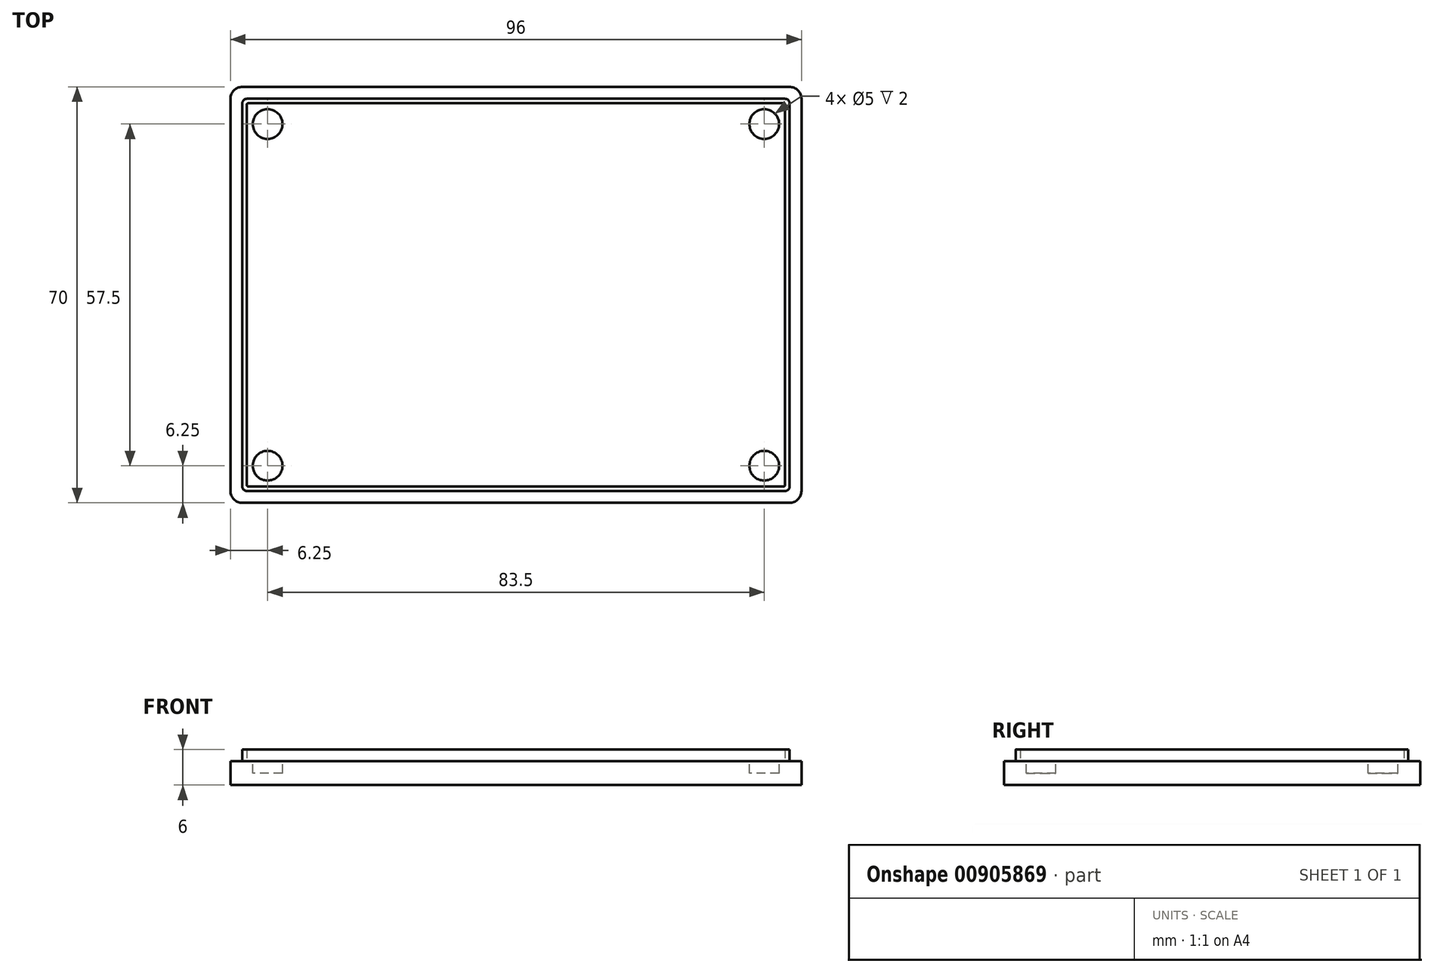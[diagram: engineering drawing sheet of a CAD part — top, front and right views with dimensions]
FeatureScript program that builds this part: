
annotation { "Feature Type Name" : "Feature", "Feature Type Description" : "" }
export const myFeature = defineFeature(function(context is Context, id is Id, definition is map)
    precondition{}
    {
        {
            var Q0;
            Q0=qCreatedBy(makeId("Top.planeOp"),FACE);
            var sketch = newSketch(context, id + "F0", { "sketchPlane" : qUnion([Q0])});
            skLineSegment(sketch, "E0.bottom", {"start": v(-46, 35) * mm, "end": v(46, 35) * mm});
            skLineSegment(sketch, "E0.top", {"start": v(-46, -35) * mm, "end": v(46, -35) * mm});
            skLineSegment(sketch, "E0.left", {"start": v(-48, 33) * mm, "end": v(-48, -33) * mm});
            skLineSegment(sketch, "E0.right", {"start": v(48, 33) * mm, "end": v(48, -33) * mm});
            skPoint(sketch, "E0.middle", {"position": v(0, 0) * mm});
            skPoint(sketch, "E1.visualSharp", {"position": v(-48, 35) * mm});
            skArc(sketch, "E1.filletArc", {"start": v(-46, 35) * mm, "mid": v(-47.41, 34.41) * mm, "end": v(-48, 33) * mm});
            skPoint(sketch, "E2.visualSharp", {"position": v(-48, -35) * mm});
            skArc(sketch, "E2.filletArc", {"start": v(-48, -33) * mm, "mid": v(-47.41, -34.41) * mm, "end": v(-46, -35) * mm});
            skPoint(sketch, "E3.visualSharp", {"position": v(48, -35) * mm});
            skArc(sketch, "E3.filletArc", {"start": v(46, -35) * mm, "mid": v(47.41, -34.41) * mm, "end": v(48, -33) * mm});
            skPoint(sketch, "E4.visualSharp", {"position": v(48, 35) * mm});
            skArc(sketch, "E4.filletArc", {"start": v(48, 33) * mm, "mid": v(47.41, 34.41) * mm, "end": v(46, 35) * mm});
            skSolve(sketch);
        }
        {
            var Q0;
            Q0=makeQuery(id+"F0.imprint","IMPRINT",FACE,{"disambiguationData":[TD([[makeQuery(id+"F0.imprint","IMPRINT",EDGE,{"derivedFrom":sQuery(id+"F0.wireOp",EDGE,"U18dfylj-Norm-gyCY-oxJm-QVkYRqjWbd2D.bottom")}),-1.0]])]});
            var Q1;
            Q1=qSketchRegion(id+"F0",true);
            extrude(context, id + "F1", {"entities" : qUnion([Q0, Q1]), "depth" : 26 * mm, "offsetDistance" : 25 * mm});
        }
        {
            var Q0;
            Q0=makeQuery(id+"F1.opExtrude","CAP_FACE",FACE,{"disambiguationData":[OSD([sQuery(id+"F0.wireOp",EDGE,"E0.bottom"),sQuery(id+"F0.wireOp",EDGE,"E0.top"),sQuery(id+"F0.wireOp",EDGE,"E0.left"),sQuery(id+"F0.wireOp",EDGE,"E0.right"),sQuery(id+"F0.wireOp",EDGE,"E1.filletArc"),sQuery(id+"F0.wireOp",EDGE,"E2.filletArc"),sQuery(id+"F0.wireOp",EDGE,"E3.filletArc"),sQuery(id+"F0.wireOp",EDGE,"E4.filletArc")])],"isStart":false});
            extrude(context, id + "F2", {"entities" : qUnion([Q0]), "depth" : 4 * mm, "offsetDistance" : 25 * mm});
        }
        {
            var Q0;
            Q0=makeQuery(id+"F1.opExtrude","CAP_FACE",FACE,{"disambiguationData":[OSD([sQuery(id+"F0.wireOp",EDGE,"E0.bottom"),sQuery(id+"F0.wireOp",EDGE,"E0.top"),sQuery(id+"F0.wireOp",EDGE,"E0.left"),sQuery(id+"F0.wireOp",EDGE,"E0.right"),sQuery(id+"F0.wireOp",EDGE,"E1.filletArc"),sQuery(id+"F0.wireOp",EDGE,"E2.filletArc"),sQuery(id+"F0.wireOp",EDGE,"E3.filletArc"),sQuery(id+"F0.wireOp",EDGE,"E4.filletArc")])],"isStart":false});
            var sketch = newSketch(context, id + "F3", { "sketchPlane" : qUnion([Q0])});
            skLineSegment(sketch, "E5.bottom", {"start": v(-45, 33) * mm, "end": v(45, 33) * mm});
            skLineSegment(sketch, "E5.top", {"start": v(-45, -33) * mm, "end": v(45, -33) * mm});
            skLineSegment(sketch, "E5.left", {"start": v(-46, 32) * mm, "end": v(-46, -32) * mm});
            skLineSegment(sketch, "E5.right", {"start": v(46, 32) * mm, "end": v(46, -32) * mm});
            skPoint(sketch, "E5.middle", {"position": v(0, 0) * mm});
            skPoint(sketch, "E6.visualSharp", {"position": v(-46, 33) * mm});
            skArc(sketch, "E6.filletArc", {"start": v(-45, 33) * mm, "mid": v(-45.7, 32.7) * mm, "end": v(-46, 32) * mm});
            skPoint(sketch, "E7.visualSharp", {"position": v(46, 33) * mm});
            skArc(sketch, "E7.filletArc", {"start": v(46, 32) * mm, "mid": v(45.7, 32.7) * mm, "end": v(45, 33) * mm});
            skPoint(sketch, "E8.visualSharp", {"position": v(46, -33) * mm});
            skArc(sketch, "E8.filletArc", {"start": v(45, -33) * mm, "mid": v(45.7, -32.7) * mm, "end": v(46, -32) * mm});
            skPoint(sketch, "E9.visualSharp", {"position": v(-46, -33) * mm});
            skArc(sketch, "E9.filletArc", {"start": v(-46, -32) * mm, "mid": v(-45.7, -32.7) * mm, "end": v(-45, -33) * mm});
            skLineSegment(sketch, "E10.bottom", {"start": v(-45, 32) * mm, "end": v(45, 32) * mm});
            skLineSegment(sketch, "E10.top", {"start": v(-45, -32) * mm, "end": v(45, -32) * mm});
            skLineSegment(sketch, "E10.left", {"start": v(-45, 32) * mm, "end": v(-45, -32) * mm});
            skLineSegment(sketch, "E10.right", {"start": v(45, 32) * mm, "end": v(45, -32) * mm});
            skSolve(sketch);
        }
        {
            var Q0;
            Q0=makeQuery(id+"F3.imprint","IMPRINT",FACE,{"disambiguationData":[TD([[makeQuery(id+"F3.imprint","IMPRINT",EDGE,{"derivedFrom":sQuery(id+"F3.wireOp",EDGE,"E5.bottom")}),-1.0]])]});
            extrude(context, id + "F4", {"entities" : qUnion([Q0]), "operationType" : NewBodyOperationType.REMOVE, "oppositeDirection" : true, "depth" : 2 * mm, "offsetDistance" : 25 * mm});
        }
        {
            var Q0;
            Q0=makeQuery(id+"F2.opExtrude","CAP_FACE",FACE,{"disambiguationData":[OSD([sQuery(id+"F0.wireOp",EDGE,"E0.bottom"),sQuery(id+"F0.wireOp",EDGE,"E0.top"),sQuery(id+"F0.wireOp",EDGE,"E0.left"),sQuery(id+"F0.wireOp",EDGE,"E0.right"),sQuery(id+"F0.wireOp",EDGE,"E1.filletArc"),sQuery(id+"F0.wireOp",EDGE,"E2.filletArc"),sQuery(id+"F0.wireOp",EDGE,"E3.filletArc"),sQuery(id+"F0.wireOp",EDGE,"E4.filletArc")])],"isStart":false});
            var sketch = newSketch(context, id + "F5", { "sketchPlane" : qUnion([Q0])});
            skLineSegment(sketch, "E11.bottom", {"start": v(-45.25, 33) * mm, "end": v(45.25, 33) * mm});
            skLineSegment(sketch, "E11.top", {"start": v(-45.25, -33) * mm, "end": v(45.25, -33) * mm});
            skLineSegment(sketch, "E11.left", {"start": v(-46, 32.25) * mm, "end": v(-46, -32.25) * mm});
            skLineSegment(sketch, "E11.right", {"start": v(46, 32.25) * mm, "end": v(46, -32.25) * mm});
            skPoint(sketch, "E11.middle", {"position": v(0, 0) * mm});
            skPoint(sketch, "E12.visualSharp", {"position": v(-46, 33) * mm});
            skArc(sketch, "E12.filletArc", {"start": v(-45.25, 33) * mm, "mid": v(-45.78, 32.78) * mm, "end": v(-46, 32.25) * mm});
            skPoint(sketch, "E13.visualSharp", {"position": v(-46, -33) * mm});
            skArc(sketch, "E13.filletArc", {"start": v(-46, -32.25) * mm, "mid": v(-45.78, -32.78) * mm, "end": v(-45.25, -33) * mm});
            skPoint(sketch, "E14.visualSharp", {"position": v(46, -33) * mm});
            skArc(sketch, "E14.filletArc", {"start": v(45.25, -33) * mm, "mid": v(45.78, -32.78) * mm, "end": v(46, -32.25) * mm});
            skPoint(sketch, "E15.visualSharp", {"position": v(46, 33) * mm});
            skArc(sketch, "E15.filletArc", {"start": v(46, 32.25) * mm, "mid": v(45.78, 32.78) * mm, "end": v(45.25, 33) * mm});
            skLineSegment(sketch, "E16.bottom", {"start": v(-45, 32.25) * mm, "end": v(45, 32.25) * mm});
            skLineSegment(sketch, "E16.top", {"start": v(-45, -32.25) * mm, "end": v(45, -32.25) * mm});
            skLineSegment(sketch, "E16.left", {"start": v(-45.25, 32) * mm, "end": v(-45.25, -32) * mm});
            skLineSegment(sketch, "E16.right", {"start": v(45.25, 32) * mm, "end": v(45.25, -32) * mm});
            skArc(sketch, "E17.filletArc", {"start": v(-45, 32.25) * mm, "mid": v(-45.18, 32.18) * mm, "end": v(-45.25, 32) * mm});
            skArc(sketch, "E18.filletArc", {"start": v(45.25, 32) * mm, "mid": v(45.18, 32.18) * mm, "end": v(45, 32.25) * mm});
            skArc(sketch, "E19.filletArc", {"start": v(45, -32.25) * mm, "mid": v(45.18, -32.18) * mm, "end": v(45.25, -32) * mm});
            skArc(sketch, "E20.filletArc", {"start": v(-45.25, -32) * mm, "mid": v(-45.18, -32.18) * mm, "end": v(-45, -32.25) * mm});
            skSolve(sketch);
        }
        {
            var Q0;
            Q0=makeQuery(id+"F5.imprint","IMPRINT",FACE,{"disambiguationData":[TD([[makeQuery(id+"F5.imprint","IMPRINT",EDGE,{"derivedFrom":sQuery(id+"F5.wireOp",EDGE,"E11.bottom")}),-1.0]])]});
            extrude(context, id + "F6", {"entities" : qUnion([Q0]), "operationType" : NewBodyOperationType.ADD, "depth" : 2 * mm, "offsetDistance" : 25 * mm});
        }
        {
            var Q0;
            Q0=makeQuery(id+"F4.boolean.opBoolean","SPLIT",FACE,{"disambiguationData":[TD([makeQuery(id+"F4.opExtrude","SWEPT_FACE",FACE,{"disambiguationData":[OSD([sQuery(id+"F3.wireOp",EDGE,"E10.bottom")])]})])],"derivedFrom":makeQuery(id+"F1.opExtrude","CAP_FACE",FACE,{"disambiguationData":[OSD([sQuery(id+"F0.wireOp",EDGE,"E0.bottom"),sQuery(id+"F0.wireOp",EDGE,"E0.top"),sQuery(id+"F0.wireOp",EDGE,"E0.left"),sQuery(id+"F0.wireOp",EDGE,"E0.right"),sQuery(id+"F0.wireOp",EDGE,"E1.filletArc"),sQuery(id+"F0.wireOp",EDGE,"E2.filletArc"),sQuery(id+"F0.wireOp",EDGE,"E3.filletArc"),sQuery(id+"F0.wireOp",EDGE,"E4.filletArc")])],"isStart":false})});
            var sketch = newSketch(context, id + "F7", { "sketchPlane" : qUnion([Q0])});
            skCircle(sketch, "E21", {"center": v(-41.5, -28.5) * mm, "radius": 2.5 * mm});
            skCircle(sketch, "E22", {"center": v(-41.5, 28.5) * mm, "radius": 2.5 * mm});
            skCircle(sketch, "E23", {"center": v(41.5, 28.5) * mm, "radius": 2.5 * mm});
            skCircle(sketch, "E24", {"center": v(41.5, -28.5) * mm, "radius": 2.5 * mm});
            skSolve(sketch);
        }
        {
            var Q0;
            Q0=makeQuery(id+"F7.imprint","IMPRINT",FACE,{"disambiguationData":[TD([[makeQuery(id+"F7.imprint","IMPRINT",EDGE,{"derivedFrom":sQuery(id+"F7.wireOp",EDGE,"E21")}),1.0]])]});
            var Q1;
            Q1=makeQuery(id+"F7.imprint","IMPRINT",FACE,{"disambiguationData":[TD([[makeQuery(id+"F7.imprint","IMPRINT",EDGE,{"derivedFrom":sQuery(id+"F7.wireOp",EDGE,"E22")}),1.0]])]});
            var Q2;
            Q2=makeQuery(id+"F7.imprint","IMPRINT",FACE,{"disambiguationData":[TD([[makeQuery(id+"F7.imprint","IMPRINT",EDGE,{"derivedFrom":sQuery(id+"F7.wireOp",EDGE,"E23")}),1.0]])]});
            var Q3;
            Q3=makeQuery(id+"F7.imprint","IMPRINT",FACE,{"disambiguationData":[TD([[makeQuery(id+"F7.imprint","IMPRINT",EDGE,{"derivedFrom":sQuery(id+"F7.wireOp",EDGE,"E24")}),1.0]])]});
            extrude(context, id + "F8", {"entities" : qUnion([Q0, Q1, Q2, Q3]), "operationType" : NewBodyOperationType.REMOVE, "oppositeDirection" : true, "depth" : 2 * mm, "offsetDistance" : 25 * mm});
        }
        {
            var Q0;
            Q0=makeQuery(id+"F6.boolean.opBoolean","SPLIT",FACE,{"disambiguationData":[TD([makeQuery(id+"F6.opExtrude","SWEPT_FACE",FACE,{"disambiguationData":[OSD([sQuery(id+"F5.wireOp",EDGE,"E16.bottom")])]})])],"derivedFrom":makeQuery(id+"F2.opExtrude","CAP_FACE",FACE,{"disambiguationData":[OSD([sQuery(id+"F0.wireOp",EDGE,"E0.bottom"),sQuery(id+"F0.wireOp",EDGE,"E0.top"),sQuery(id+"F0.wireOp",EDGE,"E0.left"),sQuery(id+"F0.wireOp",EDGE,"E0.right"),sQuery(id+"F0.wireOp",EDGE,"E1.filletArc"),sQuery(id+"F0.wireOp",EDGE,"E2.filletArc"),sQuery(id+"F0.wireOp",EDGE,"E3.filletArc"),sQuery(id+"F0.wireOp",EDGE,"E4.filletArc")])],"isStart":false})});
            var sketch = newSketch(context, id + "F9", { "sketchPlane" : qUnion([Q0])});
            skCircle(sketch, "E25", {"center": v(-41.75, 28.75) * mm, "radius": 2.5 * mm});
            skCircle(sketch, "E26", {"center": v(-41.75, -28.75) * mm, "radius": 2.5 * mm});
            skCircle(sketch, "E27", {"center": v(41.75, -28.75) * mm, "radius": 2.5 * mm});
            skCircle(sketch, "E28", {"center": v(41.75, 28.75) * mm, "radius": 2.5 * mm});
            skSolve(sketch);
        }
        {
            var Q0;
            Q0=makeQuery(id+"F9.imprint","IMPRINT",FACE,{"disambiguationData":[TD([[makeQuery(id+"F9.imprint","IMPRINT",EDGE,{"derivedFrom":sQuery(id+"F9.wireOp",EDGE,"E26")}),1.0]])]});
            var Q1;
            Q1=makeQuery(id+"F9.imprint","IMPRINT",FACE,{"disambiguationData":[TD([[makeQuery(id+"F9.imprint","IMPRINT",EDGE,{"derivedFrom":sQuery(id+"F9.wireOp",EDGE,"E25")}),1.0]])]});
            var Q2;
            Q2=makeQuery(id+"F9.imprint","IMPRINT",FACE,{"disambiguationData":[TD([[makeQuery(id+"F9.imprint","IMPRINT",EDGE,{"derivedFrom":sQuery(id+"F9.wireOp",EDGE,"E28")}),1.0]])]});
            var Q3;
            Q3=makeQuery(id+"F9.imprint","IMPRINT",FACE,{"disambiguationData":[TD([[makeQuery(id+"F9.imprint","IMPRINT",EDGE,{"derivedFrom":sQuery(id+"F9.wireOp",EDGE,"E27")}),1.0]])]});
            extrude(context, id + "F10", {"entities" : qUnion([Q0, Q1, Q2, Q3]), "operationType" : NewBodyOperationType.REMOVE, "oppositeDirection" : true, "depth" : 2 * mm, "offsetDistance" : 25 * mm});
        }
        {
            var Q0;
            Q0=makeQuery(id+"F4.boolean.opBoolean","SPLIT",FACE,{"disambiguationData":[TD([makeQuery(id+"F4.opExtrude","SWEPT_FACE",FACE,{"disambiguationData":[OSD([sQuery(id+"F3.wireOp",EDGE,"E10.bottom")])]})])],"derivedFrom":makeQuery(id+"F1.opExtrude","CAP_FACE",FACE,{"disambiguationData":[OSD([sQuery(id+"F0.wireOp",EDGE,"E0.bottom"),sQuery(id+"F0.wireOp",EDGE,"E0.top"),sQuery(id+"F0.wireOp",EDGE,"E0.left"),sQuery(id+"F0.wireOp",EDGE,"E0.right"),sQuery(id+"F0.wireOp",EDGE,"E1.filletArc"),sQuery(id+"F0.wireOp",EDGE,"E2.filletArc"),sQuery(id+"F0.wireOp",EDGE,"E3.filletArc"),sQuery(id+"F0.wireOp",EDGE,"E4.filletArc")])],"isStart":false})});
            var sketch = newSketch(context, id + "F11", { "sketchPlane" : qUnion([Q0])});
            skLineSegment(sketch, "E29.bottom", {"start": v(-43, -25) * mm, "end": v(43, -25) * mm});
            skLineSegment(sketch, "E29.top", {"start": v(-43, 25) * mm, "end": v(43, 25) * mm});
            skLineSegment(sketch, "E29.left", {"start": v(-43, -25) * mm, "end": v(-43, 25) * mm});
            skLineSegment(sketch, "E29.right", {"start": v(43, -25) * mm, "end": v(43, 25) * mm});
            skPoint(sketch, "E29.middle", {"position": v(0, 0) * mm});
            skLineSegment(sketch, "E30.bottom", {"start": v(-38, -30) * mm, "end": v(38, -30) * mm});
            skLineSegment(sketch, "E30.top", {"start": v(-38, 30) * mm, "end": v(38, 30) * mm});
            skLineSegment(sketch, "E30.left", {"start": v(-38, -30) * mm, "end": v(-38, 30) * mm});
            skLineSegment(sketch, "E30.right", {"start": v(38, -30) * mm, "end": v(38, 30) * mm});
            skSolve(sketch);
        }
        {
            var Q0;
            {var subQ0=sQuery(id+"F11.wireOp",EDGE,"E29.left");Q0=makeQuery(id+"F11.imprint","IMPRINT",FACE,{"disambiguationData":[TD([[makeQuery(id+"F11.imprint","IMPRINT",EDGE,{"derivedFrom":subQ0}),-1.0]])]});}
            var Q1;
            {var subQ5=sQuery(id+"F11.wireOp",EDGE,"E30.bottom");Q1=makeQuery(id+"F11.imprint","IMPRINT",FACE,{"disambiguationData":[TD([[makeQuery(id+"F11.imprint","IMPRINT",EDGE,{"derivedFrom":subQ5}),1.0]])]});}
            var Q2;
            {var subQ0=sQuery(id+"F11.wireOp",EDGE,"E30.left");var subQ1=sQuery(id+"F11.wireOp",EDGE,"E29.bottom");var subQ2=makeQuery(id+"F11.imprint","INTERSECT",VERTEX,{"derivedFrom":[subQ1,subQ0]});Q2=makeQuery(id+"F11.imprint","IMPRINT",FACE,{"disambiguationData":[TD([[makeQuery(id+"F11.imprint","IMPRINT",EDGE,{"disambiguationData":[TD([[subQ2,-1.0]])],"derivedFrom":subQ1}),1.0]])]});}
            var Q3;
            {var subQ5=sQuery(id+"F11.wireOp",EDGE,"E30.top");Q3=makeQuery(id+"F11.imprint","IMPRINT",FACE,{"disambiguationData":[TD([[makeQuery(id+"F11.imprint","IMPRINT",EDGE,{"derivedFrom":subQ5}),-1.0]])]});}
            var Q4;
            {var subQ0=sQuery(id+"F11.wireOp",EDGE,"E29.right");Q4=makeQuery(id+"F11.imprint","IMPRINT",FACE,{"disambiguationData":[TD([[makeQuery(id+"F11.imprint","IMPRINT",EDGE,{"derivedFrom":subQ0}),1.0]])]});}
            extrude(context, id + "F12", {"entities" : qUnion([Q0, Q1, Q2, Q3, Q4]), "operationType" : NewBodyOperationType.REMOVE, "oppositeDirection" : true, "depth" : 22 * mm, "offsetDistance" : 25 * mm});
        }
        {
            var Q0;
            Q0=makeQuery(id+"F1.opExtrude","SWEPT_FACE",FACE,{"disambiguationData":[OSD([sQuery(id+"F0.wireOp",EDGE,"E0.right")])]});
            var sketch = newSketch(context, id + "F13", { "sketchPlane" : qUnion([Q0])});
            skPoint(sketch, "E31.centerSnap0", {"position": v(-33, 13) * mm});
            skCircle(sketch, "E32", {"center": v(8, 14.5) * mm, "radius": 1 * mm});
            skPoint(sketch, "E32.centerSnap0", {"position": v(0, 0) * mm});
            skCircle(sketch, "E33", {"center": v(11, 14.5) * mm, "radius": 1 * mm});
            skCircle(sketch, "E34", {"center": v(14, 14.5) * mm, "radius": 1 * mm});
            skCircle(sketch, "E35", {"center": v(8, 11.5) * mm, "radius": 1 * mm});
            skCircle(sketch, "E36", {"center": v(11, 11.5) * mm, "radius": 1 * mm});
            skCircle(sketch, "E37", {"center": v(14, 11.5) * mm, "radius": 1 * mm});
            skSolve(sketch);
        }
        {
            var Q0;
            Q0=makeQuery(id+"F13.imprint","IMPRINT",FACE,{"disambiguationData":[TD([[makeQuery(id+"F13.imprint","IMPRINT",EDGE,{"derivedFrom":sQuery(id+"F13.wireOp",EDGE,"E32")}),1.0]])]});
            var Q1;
            Q1=makeQuery(id+"F13.imprint","IMPRINT",FACE,{"disambiguationData":[TD([[makeQuery(id+"F13.imprint","IMPRINT",EDGE,{"derivedFrom":sQuery(id+"F13.wireOp",EDGE,"E35")}),1.0]])]});
            var Q2;
            Q2=makeQuery(id+"F13.imprint","IMPRINT",FACE,{"disambiguationData":[TD([[makeQuery(id+"F13.imprint","IMPRINT",EDGE,{"derivedFrom":sQuery(id+"F13.wireOp",EDGE,"E36")}),1.0]])]});
            var Q3;
            Q3=makeQuery(id+"F13.imprint","IMPRINT",FACE,{"disambiguationData":[TD([[makeQuery(id+"F13.imprint","IMPRINT",EDGE,{"derivedFrom":sQuery(id+"F13.wireOp",EDGE,"E33")}),1.0]])]});
            var Q4;
            Q4=makeQuery(id+"F13.imprint","IMPRINT",FACE,{"disambiguationData":[TD([[makeQuery(id+"F13.imprint","IMPRINT",EDGE,{"derivedFrom":sQuery(id+"F13.wireOp",EDGE,"E34")}),1.0]])]});
            var Q5;
            Q5=makeQuery(id+"F13.imprint","IMPRINT",FACE,{"disambiguationData":[TD([[makeQuery(id+"F13.imprint","IMPRINT",EDGE,{"derivedFrom":sQuery(id+"F13.wireOp",EDGE,"E37")}),1.0]])]});
            extrude(context, id + "F14", {"entities" : qUnion([Q0, Q1, Q2, Q3, Q4, Q5]), "operationType" : NewBodyOperationType.REMOVE, "endBound" : BoundingType.UP_TO_NEXT, "oppositeDirection" : true, "depth" : 25 * mm, "offsetDistance" : 25 * mm});
        }
        {
            var Q0;
            Q0=makeQuery(id+"F1.opExtrude","SWEPT_FACE",FACE,{"disambiguationData":[OSD([sQuery(id+"F0.wireOp",EDGE,"E0.left")])]});
            var sketch = newSketch(context, id + "F15", { "sketchPlane" : qUnion([Q0])});
            skCircle(sketch, "E38", {"center": v(7, 12.5) * mm, "radius": 5 * mm});
            skCircle(sketch, "E39", {"center": v(7, 12.5) * mm, "radius": 11 * mm});
            skSolve(sketch);
        }
        {
            var Q0;
            Q0=makeQuery(id+"F15.imprint","IMPRINT",FACE,{"disambiguationData":[TD([[makeQuery(id+"F15.imprint","IMPRINT",EDGE,{"derivedFrom":sQuery(id+"F15.wireOp",EDGE,"E38")}),-1.0]])]});
            extrude(context, id + "F16", {"entities" : qUnion([Q0]), "operationType" : NewBodyOperationType.REMOVE, "oppositeDirection" : true, "depth" : 2 * mm, "offsetDistance" : 25 * mm});
        }
        {
            var Q0;
            Q0=makeQuery(id+"F15.imprint","IMPRINT",FACE,{"disambiguationData":[TD([[makeQuery(id+"F15.imprint","IMPRINT",EDGE,{"derivedFrom":sQuery(id+"F15.wireOp",EDGE,"E38")}),1.0]])]});
            extrude(context, id + "F17", {"entities" : qUnion([Q0]), "operationType" : NewBodyOperationType.REMOVE, "endBound" : BoundingType.UP_TO_NEXT, "oppositeDirection" : true, "depth" : 25 * mm, "offsetDistance" : 25 * mm});
        }
        {
            var Q0;
            Q0=makeQuery(id+"F1.opExtrude","SWEPT_FACE",FACE,{"disambiguationData":[OSD([sQuery(id+"F0.wireOp",EDGE,"E0.top")])]});
            var sketch = newSketch(context, id + "F18", { "sketchPlane" : qUnion([Q0])});
            skLineSegment(sketch, "E40.bottom", {"start": v(-33, 22) * mm, "end": v(33, 22) * mm});
            skLineSegment(sketch, "E40.top", {"start": v(-33, 4) * mm, "end": v(33, 4) * mm});
            skLineSegment(sketch, "E40.left", {"start": v(-33, 22) * mm, "end": v(-33, 4) * mm});
            skLineSegment(sketch, "E40.right", {"start": v(33, 22) * mm, "end": v(33, 4) * mm});
            skPoint(sketch, "E40.middle", {"position": v(0, 13) * mm});
            skPoint(sketch, "E40.middle.positionSnap0", {"position": v(-46, 13) * mm});
            skPoint(sketch, "E40.centerSnap0", {"position": v(-46, 13) * mm});
            skLineSegment(sketch, "E41.bottom", {"start": v(29.73, 17) * mm, "end": v(28.83, 17) * mm});
            skLineSegment(sketch, "E41.top", {"start": v(29.73, 9) * mm, "end": v(28.83, 9) * mm});
            skLineSegment(sketch, "E41.left", {"start": v(30.73, 16) * mm, "end": v(30.73, 10) * mm});
            skLineSegment(sketch, "E41.right", {"start": v(27.83, 16) * mm, "end": v(27.83, 10) * mm});
            skPoint(sketch, "E41.middle", {"position": v(29.28, 13) * mm});
            skPoint(sketch, "E41.middle.positionSnap0", {"position": v(33, 13) * mm});
            skPoint(sketch, "E41.centerSnap0", {"position": v(33, 13) * mm});
            skPoint(sketch, "E42.visualSharp", {"position": v(27.83, 9) * mm});
            skArc(sketch, "E42.filletArc", {"start": v(27.83, 10) * mm, "mid": v(28.12, 9.3) * mm, "end": v(28.83, 9) * mm});
            skPoint(sketch, "E43.visualSharp", {"position": v(27.83, 17) * mm});
            skArc(sketch, "E43.filletArc", {"start": v(28.83, 17) * mm, "mid": v(28.12, 16.7) * mm, "end": v(27.83, 16) * mm});
            skPoint(sketch, "E44.visualSharp", {"position": v(30.73, 17) * mm});
            skArc(sketch, "E44.filletArc", {"start": v(30.73, 16) * mm, "mid": v(30.44, 16.7) * mm, "end": v(29.73, 17) * mm});
            skPoint(sketch, "E45.visualSharp", {"position": v(30.73, 9) * mm});
            skArc(sketch, "E45.filletArc", {"start": v(29.73, 9) * mm, "mid": v(30.44, 9.3) * mm, "end": v(30.73, 10) * mm});
            skCircle(sketch, "E46", {"center": v(24.1, 13) * mm, "radius": 2 * mm});
            skCircle(sketch, "E47", {"center": v(17.55, 13) * mm, "radius": 2 * mm});
            skCircle(sketch, "E48", {"center": v(11, 13) * mm, "radius": 2 * mm});
            skCircle(sketch, "E49", {"center": v(-29, 13) * mm, "radius": 3 * mm});
            skCircle(sketch, "E50", {"center": v(-30.34, 6.5) * mm, "radius": 1.8 * mm});
            skCircle(sketch, "E51", {"center": v(-30.34, 6.5) * mm, "radius": 0.8 * mm});
            skCircle(sketch, "E52", {"center": v(-30.34, 19.5) * mm, "radius": 1.8 * mm});
            skCircle(sketch, "E53", {"center": v(-30.34, 19.5) * mm, "radius": 0.8 * mm});
            skCircle(sketch, "E54", {"center": v(23.84, 19.5) * mm, "radius": 1.8 * mm});
            skCircle(sketch, "E55", {"center": v(23.84, 19.5) * mm, "radius": 0.8 * mm});
            skLineSegment(sketch, "E56.bottom", {"start": v(5.2, 7.24) * mm, "end": v(-14.97, 7.24) * mm});
            skLineSegment(sketch, "E56.top", {"start": v(5.2, 18.76) * mm, "end": v(-14.97, 18.76) * mm});
            skLineSegment(sketch, "E56.left", {"start": v(5.2, 7.24) * mm, "end": v(5.2, 18.76) * mm});
            skLineSegment(sketch, "E56.right", {"start": v(-14.97, 7.24) * mm, "end": v(-14.97, 18.76) * mm});
            skPoint(sketch, "E56.middle", {"position": v(-4.89, 13) * mm});
            skSolve(sketch);
        }
        {
            var Q0;
            Q0=makeQuery(id+"F12.boolean.opBoolean","COPY",FACE,{"derivedFrom":makeQuery(id+"F12.opExtrude","SWEPT_FACE",FACE,{"disambiguationData":[OSD([sQuery(id+"F11.wireOp",EDGE,"E30.bottom")])]})});
            var sketch = newSketch(context, id + "F19", { "sketchPlane" : qUnion([Q0])});
            skLineSegment(sketch, "E57.bottom", {"start": v(32.84, 5.07) * mm, "end": v(-33.16, 5.07) * mm});
            skLineSegment(sketch, "E57.top", {"start": v(32.84, 23.07) * mm, "end": v(-33.16, 23.07) * mm});
            skLineSegment(sketch, "E57.left", {"start": v(32.84, 5.07) * mm, "end": v(32.84, 23.07) * mm});
            skLineSegment(sketch, "E57.right", {"start": v(-33.16, 5.07) * mm, "end": v(-33.16, 23.07) * mm});
            skPoint(sketch, "E57.middle", {"position": v(-0.16, 14.07) * mm});
            skPoint(sketch, "E57.middle.positionSnap0", {"position": v(45.84, 14.07) * mm});
            skPoint(sketch, "E57.centerSnap0", {"position": v(45.84, 14.07) * mm});
            skLineSegment(sketch, "E58.bottom", {"start": v(-29.9, 10.07) * mm, "end": v(-29, 10.07) * mm});
            skLineSegment(sketch, "E58.top", {"start": v(-29.9, 18.07) * mm, "end": v(-29, 18.07) * mm});
            skLineSegment(sketch, "E58.left", {"start": v(-30.9, 11.07) * mm, "end": v(-30.9, 17.07) * mm});
            skLineSegment(sketch, "E58.right", {"start": v(-28, 11.07) * mm, "end": v(-28, 17.07) * mm});
            skPoint(sketch, "E58.middle", {"position": v(-29.44, 14.07) * mm});
            skPoint(sketch, "E58.middle.positionSnap0", {"position": v(-33.16, 14.07) * mm});
            skPoint(sketch, "E58.centerSnap0", {"position": v(-33.16, 14.07) * mm});
            skPoint(sketch, "E59.visualSharp", {"position": v(-28, 18.07) * mm});
            skArc(sketch, "E59.filletArc", {"start": v(-28, 17.07) * mm, "mid": v(-28.28, 17.77) * mm, "end": v(-29, 18.07) * mm});
            skPoint(sketch, "E60.visualSharp", {"position": v(-28, 10.07) * mm});
            skArc(sketch, "E60.filletArc", {"start": v(-29, 10.07) * mm, "mid": v(-28.28, 10.36) * mm, "end": v(-28, 11.07) * mm});
            skPoint(sketch, "E61.visualSharp", {"position": v(-30.9, 10.07) * mm});
            skArc(sketch, "E61.filletArc", {"start": v(-30.9, 11.07) * mm, "mid": v(-30.6, 10.36) * mm, "end": v(-29.9, 10.07) * mm});
            skPoint(sketch, "E62.visualSharp", {"position": v(-30.9, 18.07) * mm});
            skArc(sketch, "E62.filletArc", {"start": v(-29.9, 18.07) * mm, "mid": v(-30.6, 17.77) * mm, "end": v(-30.9, 17.07) * mm});
            skCircle(sketch, "E63", {"center": v(-24.26, 14.07) * mm, "radius": 2 * mm});
            skCircle(sketch, "E64", {"center": v(-17.71, 14.07) * mm, "radius": 2 * mm});
            skCircle(sketch, "E65", {"center": v(-11.15, 14.07) * mm, "radius": 2 * mm});
            skCircle(sketch, "E66", {"center": v(28.84, 14.07) * mm, "radius": 3 * mm});
            skCircle(sketch, "E67", {"center": v(30.18, 20.57) * mm, "radius": 1.8 * mm});
            skCircle(sketch, "E68", {"center": v(30.18, 20.57) * mm, "radius": 0.8 * mm});
            skCircle(sketch, "E69", {"center": v(30.18, 7.57) * mm, "radius": 1.8 * mm});
            skCircle(sketch, "E70", {"center": v(30.18, 7.57) * mm, "radius": 0.8 * mm});
            skCircle(sketch, "E71", {"center": v(-24, 7.57) * mm, "radius": 1.8 * mm});
            skCircle(sketch, "E72", {"center": v(-24, 7.57) * mm, "radius": 0.8 * mm});
            skLineSegment(sketch, "E73.bottom", {"start": v(-5.35, 19.83) * mm, "end": v(14.8, 19.83) * mm});
            skLineSegment(sketch, "E73.top", {"start": v(-5.35, 8.3) * mm, "end": v(14.8, 8.3) * mm});
            skLineSegment(sketch, "E73.left", {"start": v(-5.35, 19.83) * mm, "end": v(-5.35, 8.3) * mm});
            skLineSegment(sketch, "E73.right", {"start": v(14.8, 19.83) * mm, "end": v(14.8, 8.3) * mm});
            skPoint(sketch, "E73.middle", {"position": v(4.73, 14.07) * mm});
            skSolve(sketch);
        }
        {
            var Q0;
            Q0=makeQuery(id+"F19.imprint","IMPRINT",FACE,{"disambiguationData":[TD([[makeQuery(id+"F19.imprint","IMPRINT",EDGE,{"derivedFrom":sQuery(id+"F19.wireOp",EDGE,"E73.bottom")}),-1.0]])]});
            var Q1;
            Q1=makeQuery(id+"F19.imprint","IMPRINT",FACE,{"disambiguationData":[TD([[makeQuery(id+"F19.imprint","IMPRINT",EDGE,{"derivedFrom":sQuery(id+"F19.wireOp",EDGE,"E66")}),1.0]])]});
            var Q2;
            Q2=makeQuery(id+"F19.imprint","IMPRINT",FACE,{"disambiguationData":[TD([[makeQuery(id+"F19.imprint","IMPRINT",EDGE,{"derivedFrom":sQuery(id+"F19.wireOp",EDGE,"E65")}),1.0]])]});
            var Q3;
            Q3=makeQuery(id+"F19.imprint","IMPRINT",FACE,{"disambiguationData":[TD([[makeQuery(id+"F19.imprint","IMPRINT",EDGE,{"derivedFrom":sQuery(id+"F19.wireOp",EDGE,"E64")}),1.0]])]});
            var Q4;
            Q4=makeQuery(id+"F19.imprint","IMPRINT",FACE,{"disambiguationData":[TD([[makeQuery(id+"F19.imprint","IMPRINT",EDGE,{"derivedFrom":sQuery(id+"F19.wireOp",EDGE,"E63")}),1.0]])]});
            var Q5;
            Q5=makeQuery(id+"F19.imprint","IMPRINT",FACE,{"disambiguationData":[TD([[makeQuery(id+"F19.imprint","IMPRINT",EDGE,{"derivedFrom":sQuery(id+"F19.wireOp",EDGE,"E58.bottom")}),1.0]])]});
            extrude(context, id + "F20", {"entities" : qUnion([Q0, Q1, Q2, Q3, Q4, Q5]), "operationType" : NewBodyOperationType.REMOVE, "endBound" : BoundingType.UP_TO_NEXT, "oppositeDirection" : true, "depth" : 25 * mm, "offsetDistance" : 25 * mm});
        }
        {
            var Q0;
            Q0=makeQuery(id+"F19.imprint","IMPRINT",FACE,{"disambiguationData":[TD([[makeQuery(id+"F19.imprint","IMPRINT",EDGE,{"derivedFrom":sQuery(id+"F19.wireOp",EDGE,"E57.bottom")}),-1.0]])]});
            extrude(context, id + "F21", {"entities" : qUnion([Q0]), "operationType" : NewBodyOperationType.REMOVE, "oppositeDirection" : true, "depth" : -3 * mm, "offsetDistance" : 25 * mm});
        }
        {
            var Q0;
            Q0=makeQuery(id+"F19.imprint","IMPRINT",FACE,{"disambiguationData":[TD([[makeQuery(id+"F19.imprint","IMPRINT",EDGE,{"derivedFrom":sQuery(id+"F19.wireOp",EDGE,"E57.bottom")}),-1.0]])]});
            extrude(context, id + "F22", {"entities" : qUnion([Q0]), "operationType" : NewBodyOperationType.REMOVE, "oppositeDirection" : true, "depth" : 3 * mm, "offsetDistance" : 25 * mm});
        }
        {
            var Q0;
            Q0=makeQuery(id+"F19.imprint","IMPRINT",FACE,{"disambiguationData":[TD([[makeQuery(id+"F19.imprint","IMPRINT",EDGE,{"derivedFrom":sQuery(id+"F19.wireOp",EDGE,"E67")}),1.0]])]});
            var Q1;
            Q1=sQuery(id+"F19.wireOp",EDGE,"E68");
            var Q2;
            Q2=sQuery(id+"F19.wireOp",EDGE,"E67");
            extrude(context, id + "F23", {"entities" : qUnion([Q0]), "operationType" : NewBodyOperationType.ADD, "surfaceEntities" : qUnion([Q1, Q2]), "depth" : 1.9 * mm, "offsetDistance" : 25 * mm});
        }
        {
            var Q0;
            Q0=makeQuery(id+"F19.imprint","IMPRINT",FACE,{"disambiguationData":[TD([[makeQuery(id+"F19.imprint","IMPRINT",EDGE,{"derivedFrom":sQuery(id+"F19.wireOp",EDGE,"E69")}),1.0]])]});
            var Q1;
            Q1=sQuery(id+"F19.wireOp",EDGE,"E70");
            var Q2;
            Q2=sQuery(id+"F19.wireOp",EDGE,"E69");
            extrude(context, id + "F24", {"entities" : qUnion([Q0]), "operationType" : NewBodyOperationType.ADD, "surfaceEntities" : qUnion([Q1, Q2]), "depth" : 1.9 * mm, "offsetDistance" : 25 * mm});
        }
        {
            var Q0;
            Q0=makeQuery(id+"F19.imprint","IMPRINT",FACE,{"disambiguationData":[TD([[makeQuery(id+"F19.imprint","IMPRINT",EDGE,{"derivedFrom":sQuery(id+"F19.wireOp",EDGE,"E71")}),1.0]])]});
            var Q1;
            Q1=sQuery(id+"F19.wireOp",EDGE,"E72");
            var Q2;
            Q2=sQuery(id+"F19.wireOp",EDGE,"E71");
            extrude(context, id + "F25", {"entities" : qUnion([Q0]), "operationType" : NewBodyOperationType.ADD, "surfaceEntities" : qUnion([Q1, Q2]), "depth" : 1.9 * mm, "offsetDistance" : 25 * mm});
        }
        {
            var Q0;
            Q0=makeQuery(id+"F2.opExtrude","CAP_FACE",FACE,{"disambiguationData":[OSD([sQuery(id+"F0.wireOp",EDGE,"E0.bottom"),sQuery(id+"F0.wireOp",EDGE,"E0.top"),sQuery(id+"F0.wireOp",EDGE,"E0.left"),sQuery(id+"F0.wireOp",EDGE,"E0.right"),sQuery(id+"F0.wireOp",EDGE,"E1.filletArc"),sQuery(id+"F0.wireOp",EDGE,"E2.filletArc"),sQuery(id+"F0.wireOp",EDGE,"E3.filletArc"),sQuery(id+"F0.wireOp",EDGE,"E4.filletArc")])],"isStart":true});
            var sketch = newSketch(context, id + "F26", { "sketchPlane" : qUnion([Q0])});
            skText(sketch, "E74", { "text": "DabNLife", "fontName": "OpenSans-Regular.ttf"});
            const initialGuessF26  = {"E74": [-0.0339, -0.02937, 0.81915, 0.57358, 0.01428]};
            skSetInitialGuess(sketch, initialGuessF26);
            skSolve(sketch);
        }
        {
            var Q0;
            Q0=makeQuery(id+"F2.opExtrude","SWEPT_BODY",BODY,{"disambiguationData":[OSD([sQuery(id+"F0.wireOp",EDGE,"E0.bottom"),sQuery(id+"F0.wireOp",EDGE,"E0.top"),sQuery(id+"F0.wireOp",EDGE,"E0.left"),sQuery(id+"F0.wireOp",EDGE,"E0.right"),sQuery(id+"F0.wireOp",EDGE,"E1.filletArc"),sQuery(id+"F0.wireOp",EDGE,"E2.filletArc"),sQuery(id+"F0.wireOp",EDGE,"E3.filletArc"),sQuery(id+"F0.wireOp",EDGE,"E4.filletArc")])]});
            transform(context, id + "F27", {"entities" : qUnion([Q0]), "transformType" : TransformType.TRANSLATION_3D, "dx" : 0 * mm, "dy" : 0 * mm, "dz" : 0 * mm, "makeCopy" : true});
        }
        {
            var Q0;
            Q0=makeQuery(id+"F27.opPattern","COPY",BODY,{"derivedFrom":makeQuery(id+"F2.opExtrude","SWEPT_BODY",BODY,{"disambiguationData":[OSD([sQuery(id+"F0.wireOp",EDGE,"E0.bottom"),sQuery(id+"F0.wireOp",EDGE,"E0.top"),sQuery(id+"F0.wireOp",EDGE,"E0.left"),sQuery(id+"F0.wireOp",EDGE,"E0.right"),sQuery(id+"F0.wireOp",EDGE,"E1.filletArc"),sQuery(id+"F0.wireOp",EDGE,"E2.filletArc"),sQuery(id+"F0.wireOp",EDGE,"E3.filletArc"),sQuery(id+"F0.wireOp",EDGE,"E4.filletArc")])]}),"instanceName":"1"});
            deleteBodies(context, id + "F28", {"entities" : qUnion([Q0])});
        }
        {
            var Q0;
            Q0=makeQuery(id+"F2.opExtrude","SWEPT_BODY",BODY,{"disambiguationData":[OSD([sQuery(id+"F0.wireOp",EDGE,"E0.bottom"),sQuery(id+"F0.wireOp",EDGE,"E0.top"),sQuery(id+"F0.wireOp",EDGE,"E0.left"),sQuery(id+"F0.wireOp",EDGE,"E0.right"),sQuery(id+"F0.wireOp",EDGE,"E1.filletArc"),sQuery(id+"F0.wireOp",EDGE,"E2.filletArc"),sQuery(id+"F0.wireOp",EDGE,"E3.filletArc"),sQuery(id+"F0.wireOp",EDGE,"E4.filletArc")])]});
            transform(context, id + "F29", {"entities" : qUnion([Q0]), "transformType" : TransformType.TRANSLATION_3D, "dx" : 0 * mm, "dy" : 0 * mm, "dz" : 0 * mm, "makeCopy" : true});
        }
        {
            var Q0;
            Q0=makeQuery(id+"F1.opExtrude","SWEPT_BODY",BODY,{"disambiguationData":[OSD([sQuery(id+"F0.wireOp",EDGE,"E0.bottom"),sQuery(id+"F0.wireOp",EDGE,"E0.top"),sQuery(id+"F0.wireOp",EDGE,"E0.left"),sQuery(id+"F0.wireOp",EDGE,"E0.right"),sQuery(id+"F0.wireOp",EDGE,"E1.filletArc"),sQuery(id+"F0.wireOp",EDGE,"E2.filletArc"),sQuery(id+"F0.wireOp",EDGE,"E3.filletArc"),sQuery(id+"F0.wireOp",EDGE,"E4.filletArc")])]});
            deleteBodies(context, id + "F30", {"entities" : qUnion([Q0])});
        }
        {
            var Q0;
            Q0=makeQuery(id+"F29.opPattern","COPY",BODY,{"derivedFrom":makeQuery(id+"F2.opExtrude","SWEPT_BODY",BODY,{"disambiguationData":[OSD([sQuery(id+"F0.wireOp",EDGE,"E0.bottom"),sQuery(id+"F0.wireOp",EDGE,"E0.top"),sQuery(id+"F0.wireOp",EDGE,"E0.left"),sQuery(id+"F0.wireOp",EDGE,"E0.right"),sQuery(id+"F0.wireOp",EDGE,"E1.filletArc"),sQuery(id+"F0.wireOp",EDGE,"E2.filletArc"),sQuery(id+"F0.wireOp",EDGE,"E3.filletArc"),sQuery(id+"F0.wireOp",EDGE,"E4.filletArc")])]}),"instanceName":"1"});
            deleteBodies(context, id + "F31", {"entities" : qUnion([Q0])});
        }
    });
